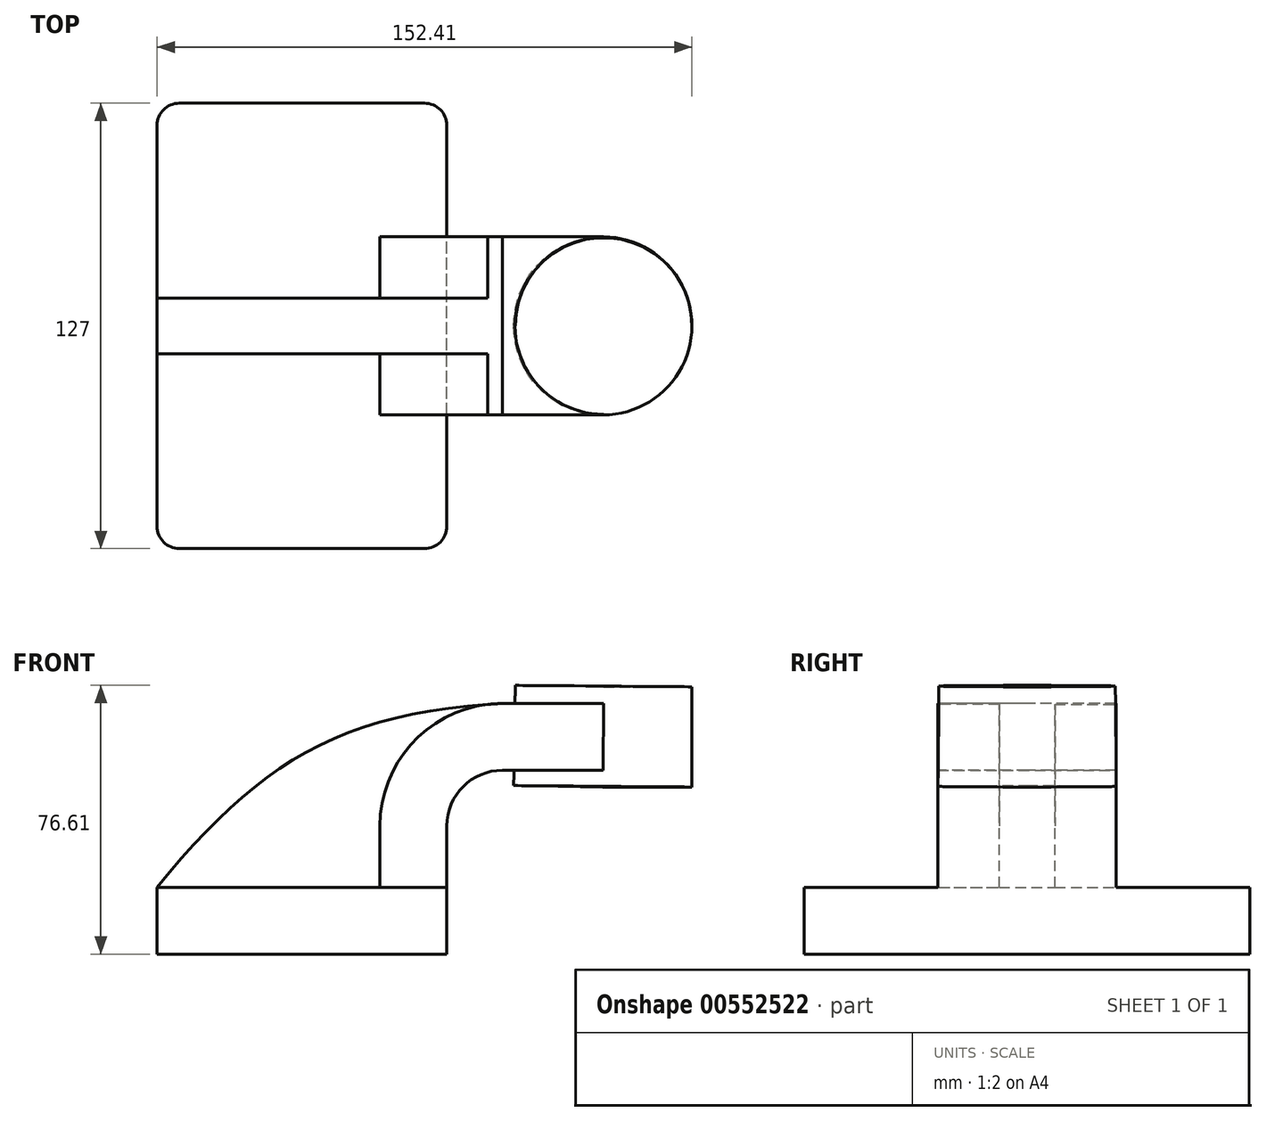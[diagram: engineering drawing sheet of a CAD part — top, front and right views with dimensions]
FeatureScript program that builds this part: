
annotation { "Feature Type Name" : "Feature", "Feature Type Description" : "" }
export const myFeature = defineFeature(function(context is Context, id is Id, definition is map)
    precondition{}
    {
        {
            var Q0;
            Q0=qCreatedBy(makeId("Front.planeOp"),FACE);
            var sketch = newSketch(context, id + "F0", { "sketchPlane" : qUnion([Q0])});
            skLineSegment(sketch, "E0.bottom", {"start": v(41.27, 9.53) * mm, "end": v(-41.28, 9.53) * mm});
            skLineSegment(sketch, "E0.top", {"start": v(41.28, -9.52) * mm, "end": v(-41.27, -9.52) * mm});
            skLineSegment(sketch, "E0.left", {"start": v(41.28, 9.53) * mm, "end": v(41.28, -9.52) * mm});
            skLineSegment(sketch, "E0.right", {"start": v(-41.28, 9.53) * mm, "end": v(-41.27, -9.52) * mm});
            skPoint(sketch, "E0.middle", {"position": v(0, 0) * mm});
            skLineSegment(sketch, "E1.bottom", {"start": v(111.12, 38.1) * mm, "end": v(60.32, 38.1) * mm});
            skLineSegment(sketch, "E1.top", {"start": v(111.12, 66.68) * mm, "end": v(60.32, 66.68) * mm});
            skLineSegment(sketch, "E1.left", {"start": v(111.12, 38.1) * mm, "end": v(111.12, 66.68) * mm});
            skLineSegment(sketch, "E1.right", {"start": v(60.32, 38.1) * mm, "end": v(60.32, 66.68) * mm});
            skPoint(sketch, "E1.middle", {"position": v(85.72, 52.39) * mm});
            skLineSegment(sketch, "E2", {"start": v(41.27, 9.53) * mm, "end": v(41.27, 27) * mm});
            skArc(sketch, "E3", {"start": v(41.27, 27) * mm, "mid": v(45.92, 38.23) * mm, "end": v(57.15, 42.88) * mm});
            skLineSegment(sketch, "E4", {"start": v(57.15, 42.88) * mm, "end": v(85.95, 42.88) * mm});
            skLineSegment(sketch, "E5.0", {"start": v(57.15, 61.93) * mm, "end": v(85.95, 61.93) * mm});
            skArc(sketch, "E5.1", {"start": v(22.23, 27) * mm, "mid": v(32.45, 51.7) * mm, "end": v(57.15, 61.93) * mm});
            skLineSegment(sketch, "E5.2", {"start": v(22.22, 9.53) * mm, "end": v(22.22, 27) * mm});
            skLineSegment(sketch, "E6", {"start": v(85.72, 38.1) * mm, "end": v(85.95, 66.68) * mm});
            skFitSpline(sketch, "E7", {"points": [v(-41.28, 9.52) * mm, v(57.15, 61.93) * mm], "startDerivative": vector(83.99, 102.93) * mm, "endDerivative": vector(142.64, 7.28) * mm});
            skSolve(sketch);
        }
        {
            var Q0;
            Q0=makeQuery(id+"F0.imprint","IMPRINT",FACE,{"disambiguationData":[TD([[makeQuery(id+"F0.imprint","IMPRINT",EDGE,{"derivedFrom":sQuery(id+"F0.wireOp",EDGE,"E0.top")}),-1.0]])]});
            extrude(context, id + "F1", {"entities" : qUnion([Q0]), "endBound" : BoundingType.SYMMETRIC, "depth" : 127 * mm, "offsetDistance" : 25.4 * mm});
        }
        {
            var Q0;
            {var subQ1=sQuery(id+"F0.wireOp",EDGE,"E2");Q0=makeQuery(id+"F0.imprint","IMPRINT",FACE,{"disambiguationData":[TD([[makeQuery(id+"F0.imprint","IMPRINT",EDGE,{"derivedFrom":subQ1}),1.0]])]});}
            var Q1;
            {var subQ0=sQuery(id+"F0.wireOp",EDGE,"E4");var subQ1=sQuery(id+"F0.wireOp",EDGE,"E1.right");var subQ2=makeQuery(id+"F0.imprint","INTERSECT",VERTEX,{"derivedFrom":[subQ1,subQ0]});Q1=makeQuery(id+"F0.imprint","IMPRINT",FACE,{"disambiguationData":[TD([[makeQuery(id+"F0.imprint","IMPRINT",EDGE,{"disambiguationData":[TD([[subQ2,-1.0]])],"derivedFrom":subQ1}),-1.0]])]});}
            extrude(context, id + "F2", {"entities" : qUnion([Q0, Q1]), "operationType" : NewBodyOperationType.ADD, "endBound" : BoundingType.SYMMETRIC, "depth" : 50.8 * mm, "offsetDistance" : 25.4 * mm});
        }
        {
            var Q0;
            {var subQ3=sQuery(id+"F0.wireOp",EDGE,"E5.2");Q0=makeQuery(id+"F0.imprint","IMPRINT",FACE,{"disambiguationData":[TD([[makeQuery(id+"F0.imprint","IMPRINT",EDGE,{"derivedFrom":subQ3}),1.0]])]});}
            extrude(context, id + "F3", {"entities" : qUnion([Q0]), "operationType" : NewBodyOperationType.ADD, "endBound" : BoundingType.SYMMETRIC, "depth" : 15.88 * mm, "offsetDistance" : 25.4 * mm});
        }
        {
            var Q0;
            {var subQ0=sQuery(id+"F0.wireOp",EDGE,"E1.left");Q0=makeQuery(id+"F0.imprint","IMPRINT",FACE,{"disambiguationData":[TD([[makeQuery(id+"F0.imprint","IMPRINT",EDGE,{"derivedFrom":subQ0}),1.0]])]});}
            var Q1;
            Q1=sQuery(id+"F0.wireOp",EDGE,"E6");
            revolve(context, id + "F4", {"operationType" : NewBodyOperationType.ADD, "entities" : qUnion([Q0]), "axis" : qUnion([Q1]), "revolveType" : RevolveType.FULL});
        }
        {
            var Q0;
            Q0=makeQuery(id+"F1.opExtrude","CAP_EDGE",EDGE,{"disambiguationData":[OSD([sQuery(id+"F0.wireOp",EDGE,"E0.left")])],"isStart":true});
            var Q1;
            Q1=makeQuery(id+"F1.opExtrude","CAP_EDGE",EDGE,{"disambiguationData":[OSD([sQuery(id+"F0.wireOp",EDGE,"E0.right")])],"isStart":true});
            var Q2;
            Q2=makeQuery(id+"F1.opExtrude","CAP_EDGE",EDGE,{"disambiguationData":[OSD([sQuery(id+"F0.wireOp",EDGE,"E0.right")])],"isStart":false});
            var Q3;
            Q3=makeQuery(id+"F1.opExtrude","CAP_EDGE",EDGE,{"disambiguationData":[OSD([sQuery(id+"F0.wireOp",EDGE,"E0.left")])],"isStart":false});
            fillet(context, id + "F5", {"entities" : qUnion([Q0, Q1, Q2, Q3]), "radius" : 6.35 * mm, "tangentPropagation" : true, "allowEdgeOverflow" : false});
        }
    });
